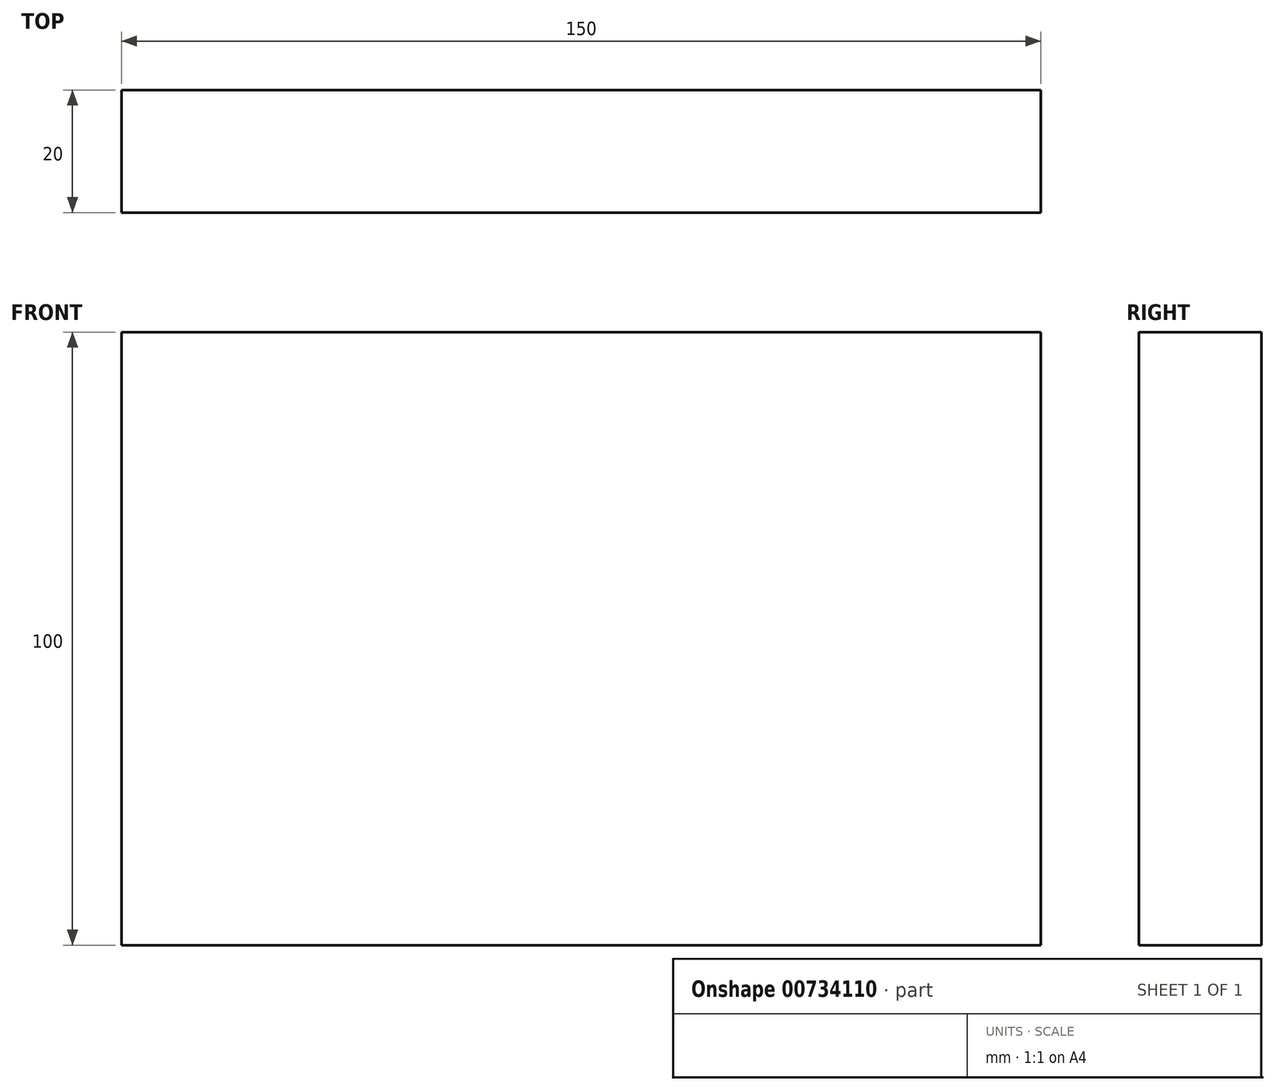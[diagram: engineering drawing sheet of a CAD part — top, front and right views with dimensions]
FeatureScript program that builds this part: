
annotation { "Feature Type Name" : "Feature", "Feature Type Description" : "" }
export const myFeature = defineFeature(function(context is Context, id is Id, definition is map)
    precondition{}
    {
        {
            var Q0;
            Q0=qCreatedBy(makeId("Front.planeOp"),FACE);
            var sketch = newSketch(context, id + "F0", { "sketchPlane" : qUnion([Q0])});
            skLineSegment(sketch, "E0.bottom", {"start": v(75, 50) * mm, "end": v(-75, 50) * mm});
            skLineSegment(sketch, "E0.top", {"start": v(75, -50) * mm, "end": v(-75, -50) * mm});
            skLineSegment(sketch, "E0.left", {"start": v(75, 50) * mm, "end": v(75, -50) * mm});
            skLineSegment(sketch, "E0.right", {"start": v(-75, 50) * mm, "end": v(-75, -50) * mm});
            skPoint(sketch, "E0.middle", {"position": v(0, 0) * mm});
            skSolve(sketch);
        }
        {
            var Q0;
            Q0 = qSketchRegion(id + "F0", true);
            extrude(context, id + "F1", {"entities" : qUnion([Q0]), "depth" : 20 * mm, "offsetDistance" : 25 * mm});
        }
    });
